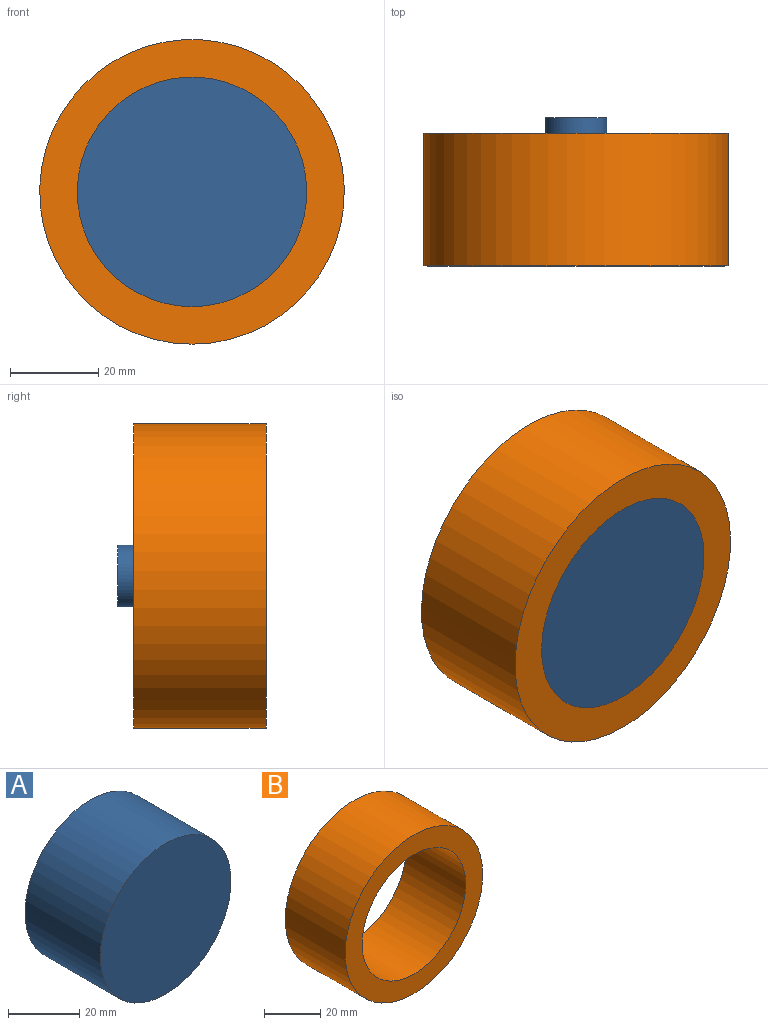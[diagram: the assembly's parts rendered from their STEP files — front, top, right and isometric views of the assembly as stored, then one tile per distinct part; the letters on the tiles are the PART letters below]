
ASSEMBLY  parts=2 mates=1
PART A: 7 faces, bbox 52x33.6x52 mm
  f0: cylinder r=26mm len=52mm, axis (0,1,0), area 4900.9mm2, adj f1,f2
  f1: plane 52x52mm, normal (0,-1,0), area 2123.7mm2, adj f0
  f2: plane 52x52mm, normal (0,1,0), area 1969.8mm2, adj f0,f3
  f3: cylinder r=7mm len=14mm, axis (0,-1,0), area 156.1mm2, adj f2,f4
  f4: plane 14x14mm, normal (0,1,0), area 146.9mm2, adj f3,f6
  f5: cone r=0mm half-angle=59deg, axis (0,1,0), area 8.2mm2, adj f6
  f6: cylinder r=1.5mm len=16mm, axis (0,1,0), area 150.8mm2, adj f4,f5
PART B: 4 faces, bbox 69x30x69 mm
  f0: cylinder r=26mm len=52mm, axis (0,1,0), area 4900.9mm2, adj f2,f3
  f1: cylinder r=34.5mm len=69mm, axis (0,1,0), area 6503.1mm2, adj f2,f3
  f2: plane 69x69mm, normal (0,-1,0), area 1615.6mm2, adj f0,f1
  f3: plane 69x69mm, normal (0,1,0), area 1615.6mm2, adj f0,f1
PLACE A t=(9.48,-102.51,18.21)mm
PLACE B t=(9.48,-102.51,18.21)mm
MATE fastened A.f0 <-> B.f0  axis (0,-1,0) through (9.48,-132.51,18.21)mm
